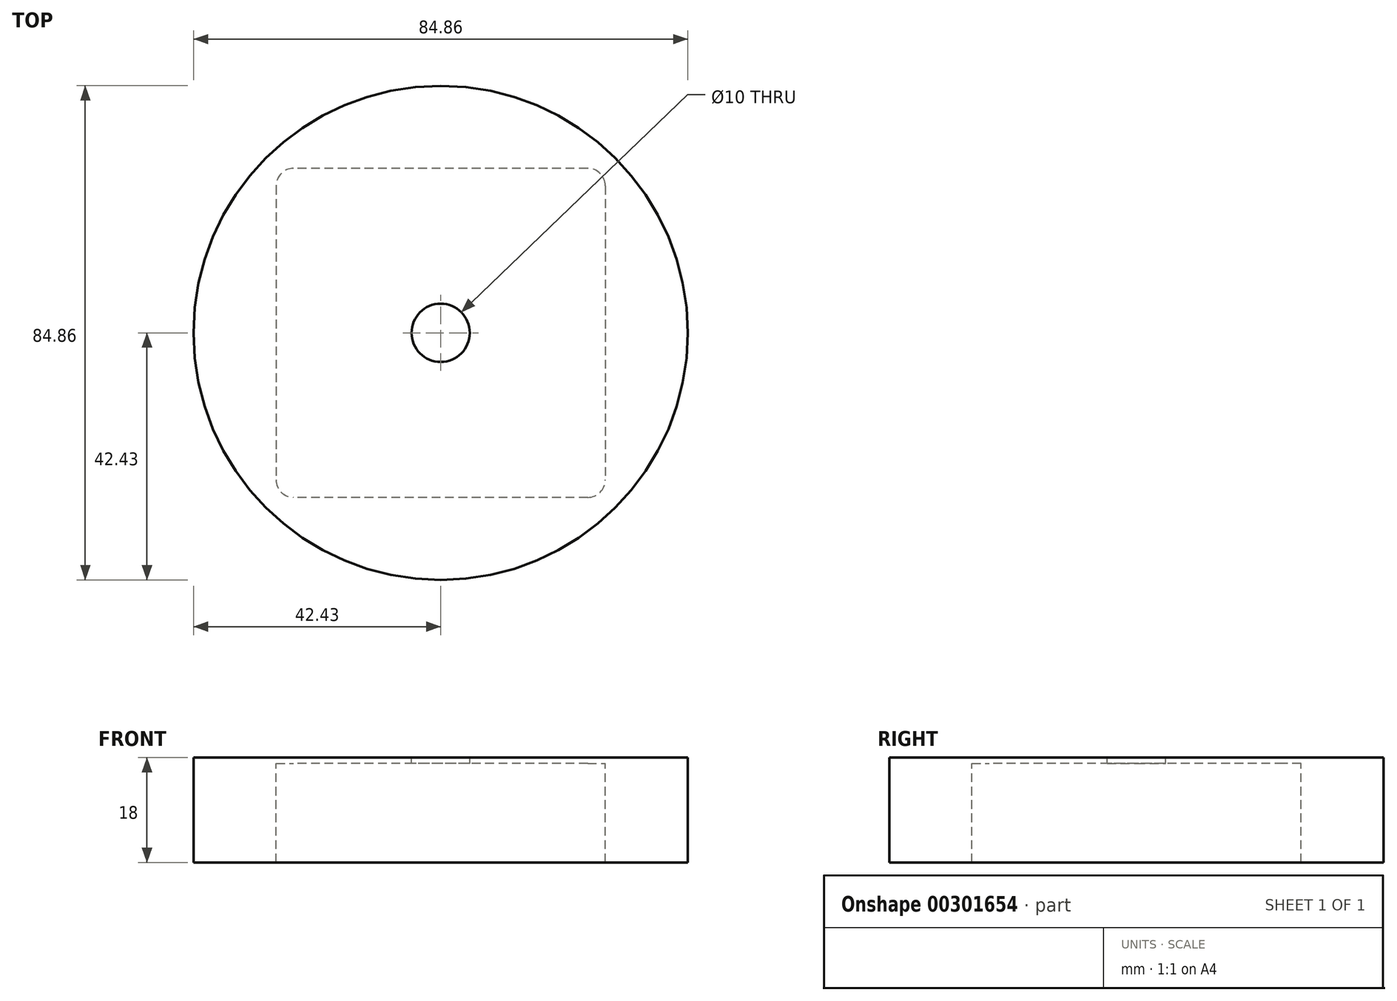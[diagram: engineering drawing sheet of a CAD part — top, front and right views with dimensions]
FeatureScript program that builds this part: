
annotation { "Feature Type Name" : "Feature", "Feature Type Description" : "" }
export const myFeature = defineFeature(function(context is Context, id is Id, definition is map)
    precondition{}
    {
        {
            var Q0;
            Q0=qCreatedBy(makeId("Top.planeOp"),FACE);
            var sketch = newSketch(context, id + "F0", { "sketchPlane" : qUnion([Q0])});
            skLineSegment(sketch, "E0.bottom", {"start": v(0, 0) * mm, "end": v(-56.5, 0) * mm});
            skLineSegment(sketch, "E0.top", {"start": v(0, -56.5) * mm, "end": v(-56.5, -56.5) * mm});
            skLineSegment(sketch, "E0.left", {"start": v(0, 0) * mm, "end": v(0, -56.5) * mm});
            skLineSegment(sketch, "E0.right", {"start": v(-56.5, 0) * mm, "end": v(-56.5, -56.5) * mm});
            skLineSegment(sketch, "E1", {"start": v(-56.5, 0) * mm, "end": v(0, -56.5) * mm, "construction": true});
            skLineSegment(sketch, "E2.bottom", {"start": v(-58.25, -58.25) * mm, "end": v(1.75, -58.25) * mm});
            skLineSegment(sketch, "E2.top", {"start": v(-58.25, 1.75) * mm, "end": v(1.75, 1.75) * mm});
            skLineSegment(sketch, "E2.left", {"start": v(-58.25, -58.25) * mm, "end": v(-58.25, 1.75) * mm});
            skLineSegment(sketch, "E2.right", {"start": v(1.75, -58.25) * mm, "end": v(1.75, 1.75) * mm});
            skPoint(sketch, "E2.middle", {"position": v(-28.25, -28.25) * mm});
            skCircle(sketch, "E3", {"center": v(-28.25, -28.25) * mm, "radius": 42.43 * mm});
            skSolve(sketch);
        }
        {
            var Q0;
            Q0=makeQuery(id+"F0.imprint","IMPRINT",FACE,{"disambiguationData":[TD([[makeQuery(id+"F0.imprint","IMPRINT",EDGE,{"derivedFrom":sQuery(id+"F0.wireOp",EDGE,"E0.bottom")}),-1.0]])]});
            extrude(context, id + "F1", {"entities" : qUnion([Q0]), "oppositeDirection" : true, "depth" : 17 * mm});
        }
        {
            var Q0;
            Q0=makeQuery(id+"F0.imprint","IMPRINT",FACE,{"disambiguationData":[TD([[makeQuery(id+"F0.imprint","IMPRINT",EDGE,{"derivedFrom":sQuery(id+"F0.wireOp",EDGE,"E0.bottom")}),-1.0]])]});
            var Q1;
            {var subQ0=sQuery(id+"F0.wireOp",EDGE,"E2.top");Q1=makeQuery(id+"F0.imprint","IMPRINT",FACE,{"disambiguationData":[TD([[makeQuery(id+"F0.imprint","IMPRINT",EDGE,{"derivedFrom":subQ0}),1.0]])]});}
            var Q2;
            {var subQ0=sQuery(id+"F0.wireOp",EDGE,"E2.right");Q2=makeQuery(id+"F0.imprint","IMPRINT",FACE,{"disambiguationData":[TD([[makeQuery(id+"F0.imprint","IMPRINT",EDGE,{"derivedFrom":subQ0}),-1.0]])]});}
            var Q3;
            {var subQ0=sQuery(id+"F0.wireOp",EDGE,"E2.bottom");Q3=makeQuery(id+"F0.imprint","IMPRINT",FACE,{"disambiguationData":[TD([[makeQuery(id+"F0.imprint","IMPRINT",EDGE,{"derivedFrom":subQ0}),-1.0]])]});}
            var Q4;
            {var subQ0=sQuery(id+"F0.wireOp",EDGE,"E2.left");Q4=makeQuery(id+"F0.imprint","IMPRINT",FACE,{"disambiguationData":[TD([[makeQuery(id+"F0.imprint","IMPRINT",EDGE,{"derivedFrom":subQ0}),1.0]])]});}
            var Q5;
            Q5=makeQuery(id+"F0.imprint","IMPRINT",FACE,{"disambiguationData":[TD([[makeQuery(id+"F0.imprint","IMPRINT",EDGE,{"derivedFrom":sQuery(id+"F0.wireOp",EDGE,"E0.bottom")}),1.0]])]});
            extrude(context, id + "F2", {"entities" : qUnion([Q0, Q1, Q2, Q3, Q4, Q5]), "operationType" : NewBodyOperationType.ADD, "depth" : 1 * mm});
        }
        {
            var Q0;
            {var subQ0=sQuery(id+"F0.wireOp",EDGE,"E2.top");Q0=makeQuery(id+"F0.imprint","IMPRINT",FACE,{"disambiguationData":[TD([[makeQuery(id+"F0.imprint","IMPRINT",EDGE,{"derivedFrom":subQ0}),1.0]])]});}
            var Q1;
            {var subQ0=sQuery(id+"F0.wireOp",EDGE,"E2.left");Q1=makeQuery(id+"F0.imprint","IMPRINT",FACE,{"disambiguationData":[TD([[makeQuery(id+"F0.imprint","IMPRINT",EDGE,{"derivedFrom":subQ0}),1.0]])]});}
            var Q2;
            {var subQ0=sQuery(id+"F0.wireOp",EDGE,"E2.right");Q2=makeQuery(id+"F0.imprint","IMPRINT",FACE,{"disambiguationData":[TD([[makeQuery(id+"F0.imprint","IMPRINT",EDGE,{"derivedFrom":subQ0}),-1.0]])]});}
            var Q3;
            {var subQ0=sQuery(id+"F0.wireOp",EDGE,"E2.bottom");Q3=makeQuery(id+"F0.imprint","IMPRINT",FACE,{"disambiguationData":[TD([[makeQuery(id+"F0.imprint","IMPRINT",EDGE,{"derivedFrom":subQ0}),-1.0]])]});}
            extrude(context, id + "F3", {"entities" : qUnion([Q0, Q1, Q2, Q3]), "operationType" : NewBodyOperationType.ADD, "oppositeDirection" : true, "depth" : 17 * mm});
        }
        {
            var Q0;
            Q0=makeQuery(id+"F2.opExtrude","CAP_FACE",FACE,{"disambiguationData":[OSD([sQuery(id+"F0.wireOp",EDGE,"E3")])],"isStart":false});
            var sketch = newSketch(context, id + "F4", { "sketchPlane" : qUnion([Q0])});
            skCircle(sketch, "E4", {"center": v(-28.25, -28.25) * mm, "radius": 5 * mm});
            skSolve(sketch);
        }
        {
            var Q0;
            Q0 = qSketchRegion(id + "F4", true);
            extrude(context, id + "F5", {"entities" : qUnion([Q0]), "operationType" : NewBodyOperationType.REMOVE, "oppositeDirection" : true, "depth" : 25 * mm});
        }
        {
            var Q0;
            Q0=makeQuery(id+"F1.opExtrude","SWEPT_EDGE",EDGE,{"disambiguationData":[OSD([sQuery(id+"F0.wireOp",EDGE,"E0.bottom"),sQuery(id+"F0.wireOp",EDGE,"E0.left")])]});
            var Q1;
            Q1=makeQuery(id+"F1.opExtrude","SWEPT_EDGE",EDGE,{"disambiguationData":[OSD([sQuery(id+"F0.wireOp",EDGE,"E0.bottom"),sQuery(id+"F0.wireOp",EDGE,"E0.right")])]});
            var Q2;
            Q2=makeQuery(id+"F1.opExtrude","SWEPT_EDGE",EDGE,{"disambiguationData":[OSD([sQuery(id+"F0.wireOp",EDGE,"E0.top"),sQuery(id+"F0.wireOp",EDGE,"E0.right")])]});
            var Q3;
            Q3=makeQuery(id+"F1.opExtrude","SWEPT_EDGE",EDGE,{"disambiguationData":[OSD([sQuery(id+"F0.wireOp",EDGE,"E0.top"),sQuery(id+"F0.wireOp",EDGE,"E0.left")])]});
            fillet(context, id + "F6", {"entities" : qUnion([Q0, Q1, Q2, Q3]), "radius" : 3 * mm, "tangentPropagation" : true, "allowEdgeOverflow" : false});
        }
    });
